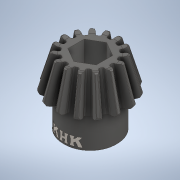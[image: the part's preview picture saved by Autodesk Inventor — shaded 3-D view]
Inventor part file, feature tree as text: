
AUTODESK INVENTOR PART (.ipt)
format: ipt  version: 2020 (Build 240168000, 168)  size: 1,507,328 bytes
history: native  units: in
note: dims shown in document units (in); Inventor stores cm internally (conversion verified against a paired STEP export)
features: extrude x1, sketch x1, imported_body x1
ambient origin geometry x8: Origin, YZ Plane, XZ Plane, XY Plane, X Axis, Y Axis, Z Axis, Center Point
bodies: Solid1 (feature_tree)
feature tree (3):
  extrude  "Extrusion1"  Depth=0.375in TaperAngle=0.0deg
  sketch  "Sketch1"  dims[d0=0.375in d1=0.3937in d2=0.0in]
  imported_body  "Base1"
